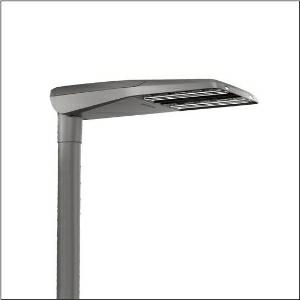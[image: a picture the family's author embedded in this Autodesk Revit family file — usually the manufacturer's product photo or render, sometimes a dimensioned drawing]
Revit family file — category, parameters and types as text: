
# Revit family: streetlight_sl_11_iq_midi___st1_2a_5xc3a51e08me_cf1e
name_source: partatom
category: Lighting Fixtures
units: mm (PartAtom-declared; Revit-internal decimal feet)

## family parameters
Cut with Voids When Loaded = No
Host = Face
Light Source = No
Part Type = Normal
Room Calculation Point = No
Round Connector Dimension = Use Diameter
Shared = No

## types (1)
- --- (1 x LED, 18110 lm, 124.7 W, 3000K)
    Apparent Load = 125 VA
    CIE Flux Codes = 32 70 96 100 100
    Color Rendering = 70
    Color Temperature = 3000K
    Default Elevation = 1800 mm
    Description = Streetlight SL 11 iQ midi, mast luminaire, primary light control with 3 zone facetted reflector, of plastic, silver coated, highly specular, primary optical cover: cover, of PMMA, transparent, light distribution: ST1.2a, light emission: direct distribution, primary light characteristic: asymmetric, installation type: post-top, side-entry, lamps: LED, High Power LED, rated values: 18.110lm | 124,7W | 145,2lm/W (begin service life); end service life: 18.110lm | 132,2W; at 50% lumin. flux: 9.055lm | 57,2W | 158,3lm/W, colour temperature: 3000K, colour rendering: CRI > 70, light colour: 730, light setting 1 begin service life: 100% | 18.110lm | 124,7W | 145,2lm/W | 3.000K, light setting 1 end service life: 132,2W, further light settings possible, control: optimised constant luminous flux control (CLO 2.0), Desk-Remote (wireless, voltage-free reading and setting of iQ features in the workshop via application-optimized NFC function/RFID function), Light-Fading, Smart-Wire, Night-Set, Lumen-Switch, Temp-Guard, Auto-Match, with cable H07RN-F 5x 1.5mm², mains connection: 230..240V, AC, 50/60Hz, connection cable pre-assembled, cable length: 12,5m, luminaire housing, of diecast aluminium, powder-coated, Siteco® metallic grey (DB 702S), please order mast flange separately, inclination adjustable without tools: 0°, 5°, 10°, 15° (post-top) | 0°, -5°, -10°, -15° (side-entry), sealing non-destructively replaceable, multi-level sealing system, length: 780mm, width: 376mm, height: 118mm, mast flange for spigot size: 42mm (side-entry): 5XC10008XM4, 60/48mm (side-entry/post-top): 5XC10108XM2, 76/60mm (side-entry/post-top): 5XC10108XM1, equipment: Power, protection rating (complete): IP66, insulation class (complete): insulation class II (safety insulation), certification: CE, ENEC, ENEC+, VDE, impact resistance: IK10, permissible operating ambient temperature for outdoor applications: -25..+50°C, standard-compliant lighting for roads and squares, Environmental Product Declaration (EPD) tested and certified by an independent institute, packaging unit: 1 piece

Light Distribution: ST1.2a
    Height = 118 mm
    Lamp = 1 x LED
    Lamp Light Flux = 18110 lm
    Lamp Power = 124.7 W
    Lamp count = 1
    Length = 780 mm
    Luminous efficacy = 145 lm/W
    Manufacturer = Siteco
    ModVariant = No
    Model = 5XC3A51E08ME
    Number of Poles = 1
    OnlyDefault = Yes
    Power Factor = 1
    Product Name = Streetlight SL 11 iQ midi | ST1.2a
    Product group = mast luminaire | pylon top
    ProductGroupID = 6100
    Protection Class = Protection class II
    Protection Degree = IP 66
    RLX_Detail_Level = 1
    RLX_Emergency_Light_Flux = 0 lm
    RLX_Emergency_Type = 0
    RLX_Emergency_Type_DB = No
    RlxData = <blob elided: 71009 chars, md5=a4002061>
    Socket = socket
    Standby Power = 0 W
    System Light Flux = 18110 lm
    System Power = 125 W
    Type Comments = factory setting: luminous flux: 100 % | dim-lin: 254 | 557 mA
    Type Image = l_1005960.jpg
    URL = http://relux.com
    VarID = @adj_217559
    Voltage = 0 V
    Weight = 0.00 kg
    Width = 376 mm

## geometry (parser evidence)
native form markers: Blend x4, Sweep x9
no freeform markers — native parametric forms only
